# Revit family: Einschub
name_source: partatom
category: HLS-Bauteile
revit_build: Autodesk Revit 2018 (Build: 20170223_1515(x64)
units: mm (PartAtom-declared; Revit-internal decimal feet)

## family parameters
Basisbauteil = Wand
Beim Laden mit Abzugskörper schneiden = Nein
Bemaßung runder Anschluss = Durchmesser verwenden
Gemeinsam genutzt = Nein
Immer vertikal = Ja
Raumberechnungspunkt = Nein
Teiletyp = Normal

## types (11) — shared parameters
H0 = 1650 mm
Rohbauöffnung = Ja
T_plate = 1.5 mm  [stored 0.00492126 ft]
Vb = 50.5 mm
Vh = 50.5 mm

## per-type parameters (varying)
| type | B | B2_Max | B2_min | B4 | B5 | B_1_3 | Bz | H | H2_Max | H2_Min | H4 | H5 | HAN | H_1_3 | Hz | T1 | T2 |
| Gipskarton25 - 600x600 | 600 mm | 610 mm | 601 mm | 579 mm | 594 mm | 599 mm | 700 mm | 600 mm | 610 mm | 601 mm | 579 mm | 594 mm | 21021 | 599 mm | 700 mm | 20 mm  [stored 0.0656168 ft] | 55 mm |
| Gipskarton25 - 500x500 | 500 mm  [stored 1.64042 ft] | 510 mm | 501 mm | 479 mm | 494 mm | 499 mm | 600 mm | 500 mm  [stored 1.64042 ft] | 510 mm | 501 mm | 479 mm | 494 mm | 20120 | 499 mm | 600 mm | 20 mm  [stored 0.0656168 ft] | 35 mm |
| Gipskarton25 - 400x400 | 400 mm  [stored 1.31234 ft] | 410 mm | 401 mm | 379 mm  [stored 1.24344 ft] | 394 mm  [stored 1.29265 ft] | 399 mm  [stored 1.30906 ft] | 500 mm  [stored 1.64042 ft] | 400 mm  [stored 1.31234 ft] | 410 mm | 401 mm | 379 mm  [stored 1.24344 ft] | 394 mm  [stored 1.29265 ft] | 21019 | 399 mm  [stored 1.30906 ft] | 500 mm  [stored 1.64042 ft] | 20 mm  [stored 0.0656168 ft] | 35 mm |
| Gipskarton25 - 800x800 | 800 mm | 810 mm | 801 mm | 779 mm | 794 mm | 799 mm | 900 mm | 800 mm | 810 mm | 801 mm | 779 mm | 794 mm | 21022 | 799 mm | 900 mm | 20 mm  [stored 0.0656168 ft] | 35 mm |
| Gipskarton25 - 300x300 | 300 mm | 310 mm | 301 mm | 279 mm | 294 mm | 299 mm | 400 mm  [stored 1.31234 ft] | 300 mm | 310 mm | 301 mm | 279 mm | 294 mm | 21018 | 299 mm | 400 mm  [stored 1.31234 ft] | 20 mm  [stored 0.0656168 ft] | 35 mm |
| Gipskarton12.5 - 200x200 | 200 mm  [stored 0.656168 ft] | 210 mm | 201 mm | 179 mm | 194 mm | 199 mm | 300 mm | 200 mm  [stored 0.656168 ft] | 210 mm | 201 mm | 179 mm | 194 mm | 21012 | 199 mm | 300 mm | 14 mm  [stored 0.0459318 ft] | 28.5 mm |
| Gipskarton12.5 - 300x300 | 300 mm | 310 mm | 301 mm | 279 mm | 294 mm | 299 mm | 400 mm  [stored 1.31234 ft] | 300 mm | 310 mm | 301 mm | 279 mm | 294 mm | 21013 | 299 mm | 400 mm  [stored 1.31234 ft] | 14 mm  [stored 0.0459318 ft] | 28.5 mm |
| Gipskarton12.5 - 400x400 | 400 mm  [stored 1.31234 ft] | 410 mm | 401 mm | 379 mm  [stored 1.24344 ft] | 394 mm  [stored 1.29265 ft] | 399 mm  [stored 1.30906 ft] | 500 mm  [stored 1.64042 ft] | 400 mm  [stored 1.31234 ft] | 410 mm | 401 mm | 379 mm  [stored 1.24344 ft] | 394 mm  [stored 1.29265 ft] | 21014 | 399 mm  [stored 1.30906 ft] | 500 mm  [stored 1.64042 ft] | 14 mm  [stored 0.0459318 ft] | 28.5 mm |
| Gipskarton12.5 - 500x500 | 500 mm  [stored 1.64042 ft] | 510 mm | 501 mm | 479 mm | 494 mm | 499 mm | 600 mm | 500 mm  [stored 1.64042 ft] | 510 mm | 501 mm | 479 mm | 494 mm | 21015 | 499 mm | 600 mm | 14 mm  [stored 0.0459318 ft] | 28.5 mm |
| Gipskarton12.5 - 600x600 | 600 mm | 610 mm | 601 mm | 579 mm | 594 mm | 599 mm | 700 mm | 600 mm | 610 mm | 601 mm | 579 mm | 594 mm | 21016 | 599 mm | 700 mm | 14 mm  [stored 0.0459318 ft] | 28.5 mm |
| Gipskarton12.5 - 800x800 | 800 mm | 810 mm | 801 mm | 779 mm | 794 mm | 799 mm | 900 mm | 800 mm | 810 mm | 801 mm | 779 mm | 794 mm | 21017 | 799 mm | 900 mm | 14 mm  [stored 0.0459318 ft] | 28.5 mm |

note: [stored X ft] marks values corroborated as IEEE doubles in the binary element streams (Revit-internal decimal feet)
